# Revit family: Shower_System-Wall_Hung-American_Standard-Flowise-1662843.002
name_source: partatom
category: Plumbing Fixtures
units: mm (PartAtom-declared; Revit-internal decimal feet)

## family parameters
Cut with Voids When Loaded = No
Host = Face
OmniClass Number = 23.45.05.14.17
OmniClass Title = Showers
Part Type = Normal
Room Calculation Point = No
Round Connector Dimension = Use Diameter
Shared = Yes

## types (1)
- 1662843.002
    59" (1500) shower hose = Yes
    Assembly Code = D2010710
    CEC Compliant = Yes
    CW Connection = No
    CWFU = 1
    Cold Water Connection Diameter = 1/2"
    Cold Water Connection Radius = 1/4"
    Connection Height = 72"
    Default Elevation = 44"
    Description = FloWise 25-In. 3-Function 2.0 GPM Shower System Kit
    Finish = Brass-American Standard-002-Polished Chrome
    Flow Rate = 2.0 gpm/7.6 Lpm
    HW Connection = No
    HWFU = 2
    Height = 23 5/8"
    Hot Water Connection Diameter = 1"
    Hot Water Connection Radius = 1/4"
    IAPMO Compliance = ASME A112.18.1, CSA 125
    Inlet Height = 70"
    Installation Instruction Link = https://lixil.cdn.celum.cloud
    Installation Type = Wall-Mounted
    Manufacturer = American Standard
    Material = Brass-American Standard-002-Polished Chrome
    Model = 1662843.002
    Price = Prices may vary. Please consult Manufacturer Representative for most up-to-date price list.
    Product Documentation Link = https://lixil.cdn.celum.cloud
    Product Page URL = https://www.americanstandard-us.com
    Tempered Water Connection = Yes
    URL = https://www.americanstandard-us.com
    Vent Connection = No
    WFU = 2
    Warranty Information = Limited 1-Year Warranty
    Waste Connection = No
    WaterSense = Yes
    Width = 5"

## geometry (parser evidence)
native form markers: Sweep x2
no freeform markers — native parametric forms only
